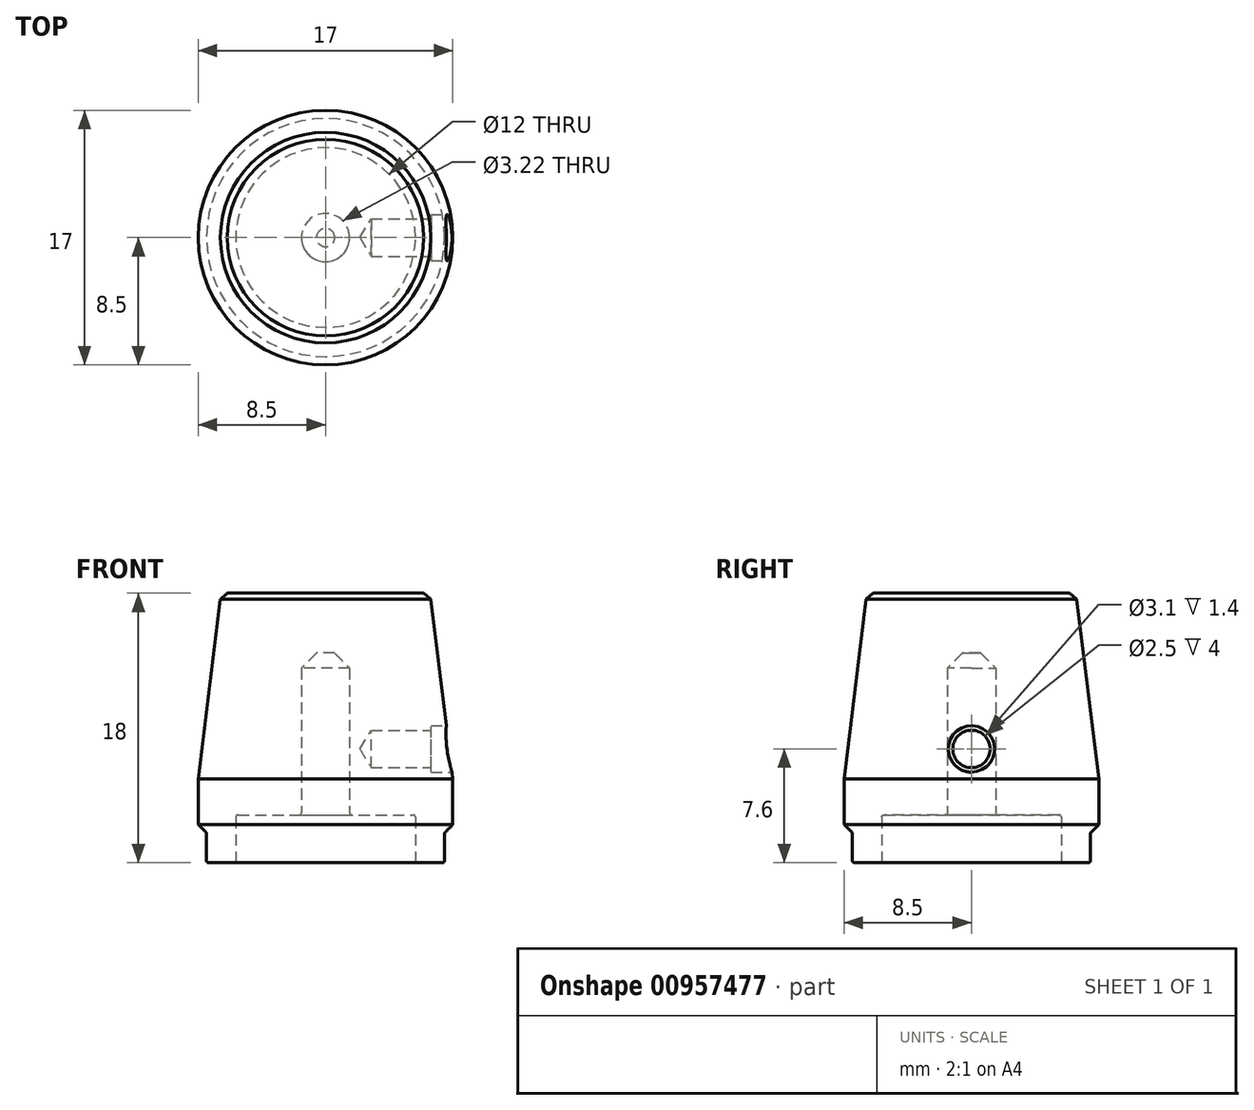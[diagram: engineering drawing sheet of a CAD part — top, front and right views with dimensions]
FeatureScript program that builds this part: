
annotation { "Feature Type Name" : "Feature", "Feature Type Description" : "" }
export const myFeature = defineFeature(function(context is Context, id is Id, definition is map)
    precondition{}
    {
        {
            var Q0;
            Q0=qCreatedBy(makeId("Front.planeOp"),FACE);
            var sketch = newSketch(context, id + "F0", { "sketchPlane" : qUnion([Q0])});
            skLineSegment(sketch, "E0.bottom", {"start": v(6, 0) * mm, "end": v(7.95, 0) * mm});
            skLineSegment(sketch, "E0.top", {"start": v(0, 18) * mm, "end": v(6.98, 18) * mm});
            skLineSegment(sketch, "E0.left", {"start": v(0, 3.2) * mm, "end": v(0, 18) * mm, "construction": true});
            skLineSegment(sketch, "E0.right", {"start": v(8.5, 2) * mm, "end": v(8.5, 5.6) * mm});
            skLineSegment(sketch, "E1", {"start": v(1.6, 3.2) * mm, "end": v(6, 3.2) * mm});
            skLineSegment(sketch, "E2", {"start": v(6, 3.2) * mm, "end": v(6, 0) * mm});
            skLineSegment(sketch, "E3", {"start": v(7.95, 0) * mm, "end": v(7.95, 2) * mm});
            skLineSegment(sketch, "E4", {"start": v(7.95, 2) * mm, "end": v(8.5, 2) * mm});
            skLineSegment(sketch, "E5", {"start": v(1.6, 3.2) * mm, "end": v(1.6, 14) * mm});
            skLineSegment(sketch, "E6", {"start": v(1.6, 14) * mm, "end": v(0, 14) * mm});
            skLineSegment(sketch, "E7", {"start": v(0, 18) * mm, "end": v(0, 14) * mm});
            skPoint(sketch, "E8", {"position": v(0, 7.6) * mm});
            skLineSegment(sketch, "E9", {"start": v(6.98, 18) * mm, "end": v(8.5, 5.6) * mm});
            skLineSegment(sketch, "E10", {"start": v(8.5, 5.6) * mm, "end": v(8.5, 20.36) * mm, "construction": true});
            skPoint(sketch, "E11", {"position": v(0, 0) * mm});
            skLineSegment(sketch, "E12", {"start": v(0, 7.6) * mm, "end": v(8.5, 7.6) * mm, "construction": true});
            skPoint(sketch, "E13", {"position": v(8.5, 7.6) * mm});
            skSolve(sketch);
        }
        {
            var Q0;
            Q0=qSketchRegion(id+"F0",true);
            var Q1;
            Q1=sQuery(id+"F0.wireOp",EDGE,"E0.left");
            revolve(context, id + "F1", {"entities" : qUnion([Q0]), "axis" : qUnion([Q1]), "revolveType" : RevolveType.FULL});
        }
        {
            var Q0;
            Q0=makeQuery(id+"F1.opRevolve","SWEPT_EDGE",EDGE,{"disambiguationData":[OSD([sQuery(id+"F0.wireOp",EDGE,"E0.right"),sQuery(id+"F0.wireOp",EDGE,"E4")])]});
            chamfer(context, id + "F2", {"entities" : qUnion([Q0]), "width" : .55 * mm});
        }
        {
            var Q0;
            Q0=makeQuery(id+"F1.opRevolve","SWEPT_EDGE",EDGE,{"disambiguationData":[OSD([sQuery(id+"F0.wireOp",EDGE,"E5"),sQuery(id+"F0.wireOp",EDGE,"E6")])]});
            chamfer(context, id + "F3", {"entities" : qUnion([Q0]), "width" : 1 * mm, "tangentPropagation" : true});
        }
        {
            var Q0;
            Q0=makeQuery(id+"F1.opRevolve","SWEPT_EDGE",EDGE,{"disambiguationData":[OSD([sQuery(id+"F0.wireOp",EDGE,"E0.top"),sQuery(id+"F0.wireOp",EDGE,"E9")])]});
            chamfer(context, id + "F4", {"entities" : qUnion([Q0]), "width" : .47 * mm, "tangentPropagation" : true});
        }
        {
            var Q0;
            Q0=makeQuery(id+"F1.opRevolve","SWEPT_FACE",FACE,{"disambiguationData":[OSD([sQuery(id+"F0.wireOp",EDGE,"E0.bottom")])]});
            var Q1;
            Q1=makeQuery(id+"F1.opRevolve","SWEPT_EDGE",EDGE,{"disambiguationData":[OSD([sQuery(id+"F0.wireOp",EDGE,"E1"),sQuery(id+"F0.wireOp",EDGE,"E2")])]});
            var Q2;
            Q2=makeQuery(id+"F1.opRevolve","SWEPT_EDGE",EDGE,{"disambiguationData":[OSD([sQuery(id+"F0.wireOp",EDGE,"E1"),sQuery(id+"F0.wireOp",EDGE,"E5")])]});
            var Q3;
            Q3=makeQuery(id+"F2.opChamfer","BLEND_EDGE",EDGE,{"blendedFrom":[makeQuery(id+"F1.opRevolve","SWEPT_EDGE",EDGE,{"disambiguationData":[OSD([sQuery(id+"F0.wireOp",EDGE,"E0.right"),sQuery(id+"F0.wireOp",EDGE,"E4")])]}),makeQuery(id+"F1.opRevolve","SWEPT_FACE",FACE,{"disambiguationData":[OSD([sQuery(id+"F0.wireOp",EDGE,"E3")])]})],"blendedInto":[makeQuery(id+"F1.opRevolve","SWEPT_FACE",FACE,{"disambiguationData":[OSD([sQuery(id+"F0.wireOp",EDGE,"E3")])]})]});
            fillet(context, id + "F5", {"entities" : qUnion([Q0, Q1, Q2, Q3]), "radius" : 0.15 * mm, "tangentPropagation" : true, "allowEdgeOverflow" : false});
        }
        {
            var Q0;
            Q0=sQuery(id+"F0.wireOp",EDGE,"E0.right");
            cPlane(context, id + "F6", {"entities" : qUnion([Q0]), "cplaneType" : CPlaneType.LINE_ANGLE, "offset" : 25 * mm, "angle" : 0 * degree, "width" : 150 * mm, "height" : 150 * mm});
        }
        {
            var Q0;
            Q0=qCreatedBy(id+"F6.planeOp",FACE);
            var sketch = newSketch(context, id + "F7", { "sketchPlane" : qUnion([Q0])});
            skPoint(sketch, "E14.0", {"position": v(0, 7.6) * mm});
            skSolve(sketch);
        }
        {
            var Q0;
            Q0=sQuery(id+"F7.wireOp",VERTEX,"E14.0");
            var Q1;
            Q1=makeQuery(id+"F1.opRevolve","SWEPT_BODY",BODY,{"disambiguationData":[OSD([sQuery(id+"F0.wireOp",EDGE,"E0.bottom"),sQuery(id+"F0.wireOp",EDGE,"E0.top"),sQuery(id+"F0.wireOp",EDGE,"E0.right"),sQuery(id+"F0.wireOp",EDGE,"E1"),sQuery(id+"F0.wireOp",EDGE,"E2"),sQuery(id+"F0.wireOp",EDGE,"E3"),sQuery(id+"F0.wireOp",EDGE,"E4"),sQuery(id+"F0.wireOp",EDGE,"E5"),sQuery(id+"F0.wireOp",EDGE,"E6"),sQuery(id+"F0.wireOp",EDGE,"E7"),sQuery(id+"F0.wireOp",EDGE,"E9")])]});
            hole(context, id + "F8", {"style" : HoleStyle.C_BORE, "endStyle" : HoleEndStyle.BLIND, "holeDiameter" : 2.5 * mm, "cBoreDiameter" : 3.1 * mm, "cBoreDepth" : 1 * mm, "holeDepth" : 5 * mm, "isTappedThrough" : true, "tappedDepth" : 12 * mm, "tapClearance" : 3, "locations" : qUnion([Q0]), "scope" : qUnion([Q1])});
        }
    });
